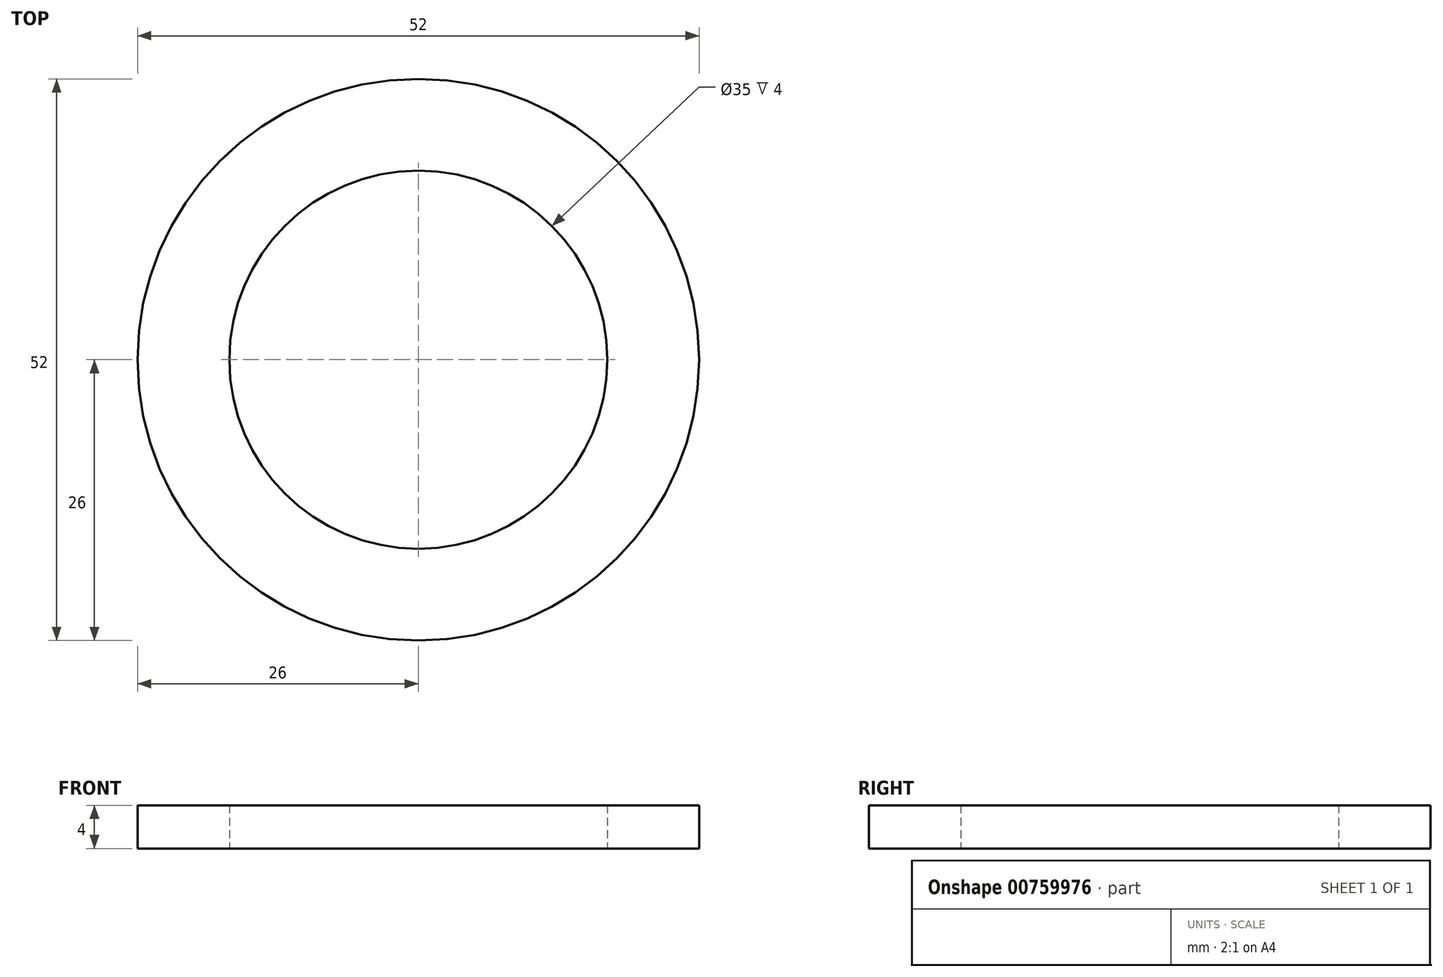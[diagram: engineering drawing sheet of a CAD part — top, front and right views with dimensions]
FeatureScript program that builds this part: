
annotation { "Feature Type Name" : "Feature", "Feature Type Description" : "" }
export const myFeature = defineFeature(function(context is Context, id is Id, definition is map)
    precondition{}
    {
        {
            var Q0;
            Q0=qCreatedBy(makeId("Top.planeOp"),FACE);
            var sketch = newSketch(context, id + "F0", { "sketchPlane" : qUnion([Q0])});
            skCircle(sketch, "E0", {"center": v(0, 0) * mm, "radius": 17.5 * mm});
            skCircle(sketch, "E1", {"center": v(0, 0) * mm, "radius": 26 * mm});
            skSolve(sketch);
        }
        {
            var Q0;
            Q0=makeQuery(id+"F0.imprint","IMPRINT",FACE,{"disambiguationData":[TD([[makeQuery(id+"F0.imprint","IMPRINT",EDGE,{"derivedFrom":sQuery(id+"F0.wireOp",EDGE,"E0")}),-1.0]])]});
            extrude(context, id + "F1", {"entities" : qUnion([Q0]), "depth" : 4 * mm, "offsetDistance" : 25 * mm});
        }
    });
